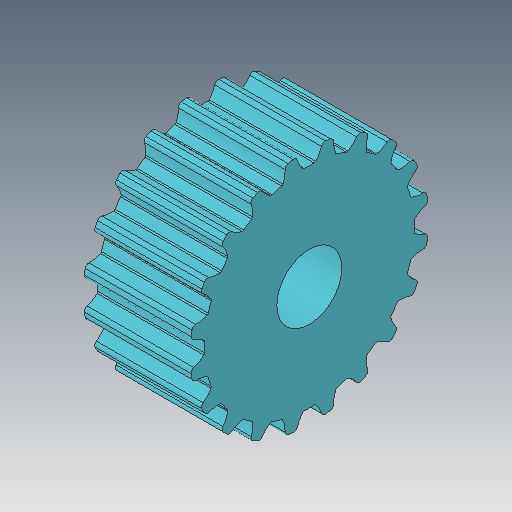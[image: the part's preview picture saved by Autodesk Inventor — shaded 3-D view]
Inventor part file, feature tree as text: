
AUTODESK INVENTOR PART (.ipt)
format: ipt  version: 2019.4 (Build 234330000, 330)  size: 279,040 bytes
history: native  units: mm
features: sketch x3, fillet x2, other x1, extrude x1, pattern_circular x1, hole x1
ambient origin geometry x8: Origin, YZ Plane, XZ Plane, XY Plane, X Axis, Y Axis, Z Axis, Center Point
bodies: Body1 (feature_tree)
feature tree (9):
  other  "ソリッド1"
  extrude  "押し出し1"  Depth=1.95mm
  fillet  "フィレット1"  Radius=1.975mm
  fillet  "フィレット2"  Radius=1.11mm
  pattern_circular  "円形状パターン1"  [2 undecoded]
  hole  "穴1"  [1 undecoded]
  sketch  "スケッチ3"
  sketch  "スケッチ1"
  sketch  "スケッチ2"
note: 3 required parameter values undecoded (feature->parameter linkage not recoverable at this tier; creation-order binding heuristic only, values carry confidence <= 0.55)
